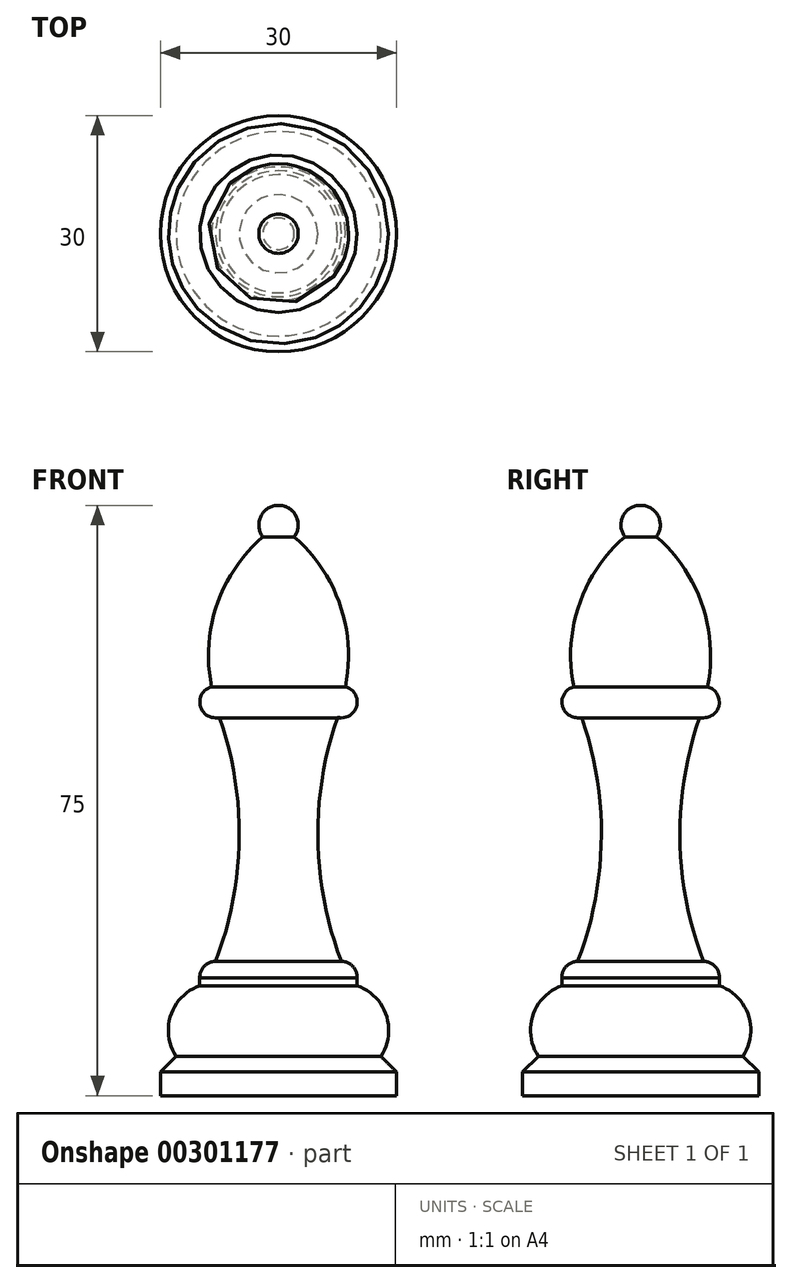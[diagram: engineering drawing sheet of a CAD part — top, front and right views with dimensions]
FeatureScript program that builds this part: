
annotation { "Feature Type Name" : "Feature", "Feature Type Description" : "" }
export const myFeature = defineFeature(function(context is Context, id is Id, definition is map)
    precondition{}
    {
        {
            var Q0;
            Q0=qCreatedBy(makeId("Front.planeOp"),FACE);
            var sketch = newSketch(context, id + "F0", { "sketchPlane" : qUnion([Q0])});
            skLineSegment(sketch, "E0", {"start": v(0, 0) * mm, "end": v(0, -75) * mm});
            skArc(sketch, "E1", {"start": v(2, -4) * mm, "mid": v(2.24, -1.38) * mm, "end": v(0, 0) * mm});
            skArc(sketch, "E2", {"start": v(8.5, -23.06) * mm, "mid": v(7.82, -12.65) * mm, "end": v(2, -4) * mm});
            skArc(sketch, "E3", {"start": v(7.5, -26.93) * mm, "mid": v(9.94, -25.5) * mm, "end": v(8.5, -23.06) * mm});
            skArc(sketch, "E4", {"start": v(7.5, -26.93) * mm, "mid": v(5, -42.49) * mm, "end": v(8, -57.95) * mm});
            skArc(sketch, "E5", {"start": v(10, -60.03) * mm, "mid": v(9.44, -58.57) * mm, "end": v(8, -57.95) * mm});
            skLineSegment(sketch, "E6", {"start": v(10, -60.03) * mm, "end": v(10, -61.03) * mm});
            skArc(sketch, "E7", {"start": v(13, -70) * mm, "mid": v(13.69, -64.78) * mm, "end": v(10, -61.03) * mm});
            skLineSegment(sketch, "E8", {"start": v(13, -70) * mm, "end": v(15, -72) * mm});
            skLineSegment(sketch, "E9", {"start": v(15, -72) * mm, "end": v(15, -75) * mm});
            skLineSegment(sketch, "E10", {"start": v(15, -75) * mm, "end": v(0, -75) * mm});
            skSolve(sketch);
        }
        {
            var Q0;
            Q0=makeQuery(id+"F0.imprint","IMPRINT",FACE,{"disambiguationData":[TD([[makeQuery(id+"F0.imprint","IMPRINT",EDGE,{"derivedFrom":sQuery(id+"F0.wireOp",EDGE,"E0")}),1.0]])]});
            var Q1;
            Q1=sQuery(id+"F0.wireOp",EDGE,"E0");
            revolve(context, id + "F1", {"entities" : qUnion([Q0]), "axis" : qUnion([Q1]), "revolveType" : RevolveType.FULL});
        }
    });
